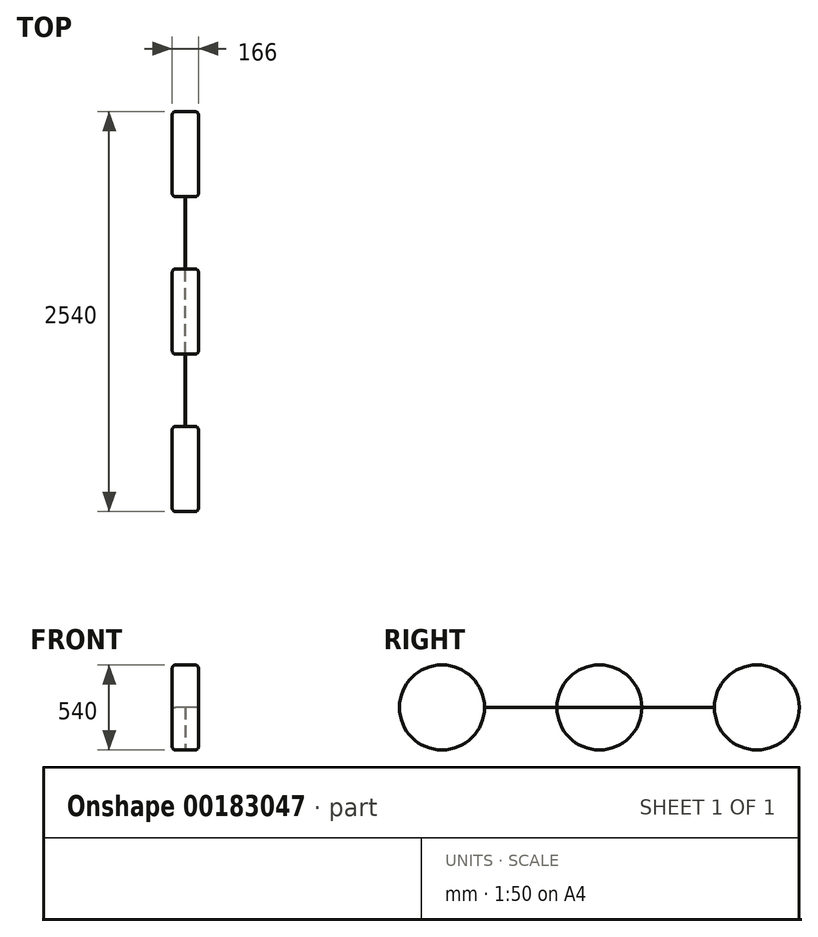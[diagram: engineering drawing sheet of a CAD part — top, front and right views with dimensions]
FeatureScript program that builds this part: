
annotation { "Feature Type Name" : "Feature", "Feature Type Description" : "" }
export const myFeature = defineFeature(function(context is Context, id is Id, definition is map)
    precondition{}
    {
        {
            var Q0;
            Q0=qCreatedBy(makeId("Right.planeOp"),FACE);
            var sketch = newSketch(context, id + "F0", { "sketchPlane" : qUnion([Q0])});
            skCircle(sketch, "E0", {"center": v(-534.92, 0) * mm, "radius": 270 * mm});
            skCircle(sketch, "E1", {"center": v(465.08, 0) * mm, "radius": 270 * mm});
            skCircle(sketch, "E2", {"center": v(1465.08, 0) * mm, "radius": 270 * mm});
            skLineSegment(sketch, "E3.bottom", {"start": v(-534.92, 0) * mm, "end": v(1465.08, 0) * mm});
            skLineSegment(sketch, "E3.top", {"start": v(-534.92, 1) * mm, "end": v(1465.08, 1) * mm});
            skLineSegment(sketch, "E3.left", {"start": v(-534.92, 0) * mm, "end": v(-534.92, 1) * mm});
            skLineSegment(sketch, "E3.right", {"start": v(1465.08, 0) * mm, "end": v(1465.08, 1) * mm});
            skSolve(sketch);
        }
        {
            var Q0;
            {var subQ5=sQuery(id+"F0.wireOp",EDGE,"E3.left");Q0=makeQuery(id+"F0.imprint","IMPRINT",FACE,{"disambiguationData":[TD([[makeQuery(id+"F0.imprint","IMPRINT",EDGE,{"derivedFrom":subQ5}),1.0]])]});}
            var Q1;
            {var subQ0=sQuery(id+"F0.wireOp",EDGE,"E3.top");var subQ1=sQuery(id+"F0.wireOp",EDGE,"E1");var subQ2=makeQuery(id+"F0.imprint","INTERSECT",VERTEX,{"disambiguationData":[OD(0.0)],"derivedFrom":[subQ1,subQ0]});Q1=makeQuery(id+"F0.imprint","IMPRINT",FACE,{"disambiguationData":[TD([[makeQuery(id+"F0.imprint","IMPRINT",EDGE,{"disambiguationData":[TD([[subQ2,-1.0]])],"derivedFrom":subQ1}),1.0]])]});}
            var Q2;
            {var subQ5=sQuery(id+"F0.wireOp",EDGE,"E3.right");Q2=makeQuery(id+"F0.imprint","IMPRINT",FACE,{"disambiguationData":[TD([[makeQuery(id+"F0.imprint","IMPRINT",EDGE,{"derivedFrom":subQ5}),-1.0]])]});}
            var Q3;
            {var subQ5=sQuery(id+"F0.wireOp",EDGE,"E3.right");Q3=makeQuery(id+"F0.imprint","IMPRINT",FACE,{"disambiguationData":[TD([[makeQuery(id+"F0.imprint","IMPRINT",EDGE,{"derivedFrom":subQ5}),1.0]])]});}
            var Q4;
            {var subQ0=sQuery(id+"F0.wireOp",EDGE,"E3.bottom");var subQ1=sQuery(id+"F0.wireOp",EDGE,"E1");var subQ2=makeQuery(id+"F0.imprint","INTERSECT",VERTEX,{"disambiguationData":[OD(0.0)],"derivedFrom":[subQ1,subQ0]});Q4=makeQuery(id+"F0.imprint","IMPRINT",FACE,{"disambiguationData":[TD([[makeQuery(id+"F0.imprint","IMPRINT",EDGE,{"disambiguationData":[TD([[subQ2,1.0]])],"derivedFrom":subQ1}),1.0]])]});}
            var Q5;
            {var subQ0=sQuery(id+"F0.wireOp",EDGE,"E3.top");var subQ1=sQuery(id+"F0.wireOp",EDGE,"E1");var subQ2=makeQuery(id+"F0.imprint","INTERSECT",VERTEX,{"disambiguationData":[OD(0.0)],"derivedFrom":[subQ1,subQ0]});Q5=makeQuery(id+"F0.imprint","IMPRINT",FACE,{"disambiguationData":[TD([[makeQuery(id+"F0.imprint","IMPRINT",EDGE,{"disambiguationData":[TD([[subQ2,1.0]])],"derivedFrom":subQ1}),1.0]])]});}
            var Q6;
            {var subQ5=sQuery(id+"F0.wireOp",EDGE,"E3.left");Q6=makeQuery(id+"F0.imprint","IMPRINT",FACE,{"disambiguationData":[TD([[makeQuery(id+"F0.imprint","IMPRINT",EDGE,{"derivedFrom":subQ5}),-1.0]])]});}
            extrude(context, id + "F1", {"entities" : qUnion([Q0, Q1, Q2, Q3, Q4, Q5, Q6]), "endBound" : BoundingType.SYMMETRIC, "depth" : 166 * mm});
        }
        {
            var Q0;
            Q0=makeQuery(id+"F1.opExtrude","CAP_EDGE",EDGE,{"disambiguationData":[OSD([sQuery(id+"F0.wireOp",EDGE,"E0")])],"isStart":false});
            var Q1;
            Q1=makeQuery(id+"F1.opExtrude","CAP_EDGE",EDGE,{"disambiguationData":[OSD([sQuery(id+"F0.wireOp",EDGE,"E0")])],"isStart":true});
            var Q2;
            {var subQ0=sQuery(id+"F0.wireOp",EDGE,"E3.top");var subQ1=sQuery(id+"F0.wireOp",EDGE,"E1");Q2=makeQuery(id+"F1.opExtrude","CAP_EDGE",EDGE,{"disambiguationData":[OSD([subQ1]),TDD([makeQuery(id+"F0.imprint","IMPRINT",EDGE,{"disambiguationData":[TD([[makeQuery(id+"F0.imprint","INTERSECT",VERTEX,{"disambiguationData":[OD(0.0)],"derivedFrom":[subQ1,subQ0]}),-1.0]])],"derivedFrom":subQ1})])],"isStart":false});}
            var Q3;
            {var subQ0=sQuery(id+"F0.wireOp",EDGE,"E3.top");var subQ1=sQuery(id+"F0.wireOp",EDGE,"E1");Q3=makeQuery(id+"F1.opExtrude","CAP_EDGE",EDGE,{"disambiguationData":[OSD([subQ1]),TDD([makeQuery(id+"F0.imprint","IMPRINT",EDGE,{"disambiguationData":[TD([[makeQuery(id+"F0.imprint","INTERSECT",VERTEX,{"disambiguationData":[OD(0.0)],"derivedFrom":[subQ1,subQ0]}),-1.0]])],"derivedFrom":subQ1})])],"isStart":true});}
            var Q4;
            {var subQ0=sQuery(id+"F0.wireOp",EDGE,"E3.bottom");var subQ1=sQuery(id+"F0.wireOp",EDGE,"E1");Q4=makeQuery(id+"F1.opExtrude","CAP_EDGE",EDGE,{"disambiguationData":[OSD([subQ1]),TDD([makeQuery(id+"F0.imprint","IMPRINT",EDGE,{"disambiguationData":[TD([[makeQuery(id+"F0.imprint","INTERSECT",VERTEX,{"disambiguationData":[OD(0.0)],"derivedFrom":[subQ1,subQ0]}),1.0]])],"derivedFrom":subQ1})])],"isStart":false});}
            var Q5;
            Q5=makeQuery(id+"F1.opExtrude","CAP_EDGE",EDGE,{"disambiguationData":[OSD([sQuery(id+"F0.wireOp",EDGE,"E2")])],"isStart":false});
            var Q6;
            Q6=makeQuery(id+"F1.opExtrude","CAP_EDGE",EDGE,{"disambiguationData":[OSD([sQuery(id+"F0.wireOp",EDGE,"E2")])],"isStart":true});
            var Q7;
            {var subQ0=sQuery(id+"F0.wireOp",EDGE,"E3.bottom");var subQ1=sQuery(id+"F0.wireOp",EDGE,"E1");Q7=makeQuery(id+"F1.opExtrude","CAP_EDGE",EDGE,{"disambiguationData":[OSD([subQ1]),TDD([makeQuery(id+"F0.imprint","IMPRINT",EDGE,{"disambiguationData":[TD([[makeQuery(id+"F0.imprint","INTERSECT",VERTEX,{"disambiguationData":[OD(0.0)],"derivedFrom":[subQ1,subQ0]}),1.0]])],"derivedFrom":subQ1})])],"isStart":true});}
            fillet(context, id + "F2", {"entities" : qUnion([Q0, Q1, Q2, Q3, Q4, Q5, Q6, Q7]), "radius" : 20 * mm, "tangentPropagation" : true, "allowEdgeOverflow" : false});
        }
        {
            var Q0;
            Q0=qSketchRegion(id+"F0",true);
            extrude(context, id + "F3", {"entities" : qUnion([Q0]), "operationType" : NewBodyOperationType.ADD, "endBound" : BoundingType.SYMMETRIC, "depth" : 1 * mm});
        }
    });
